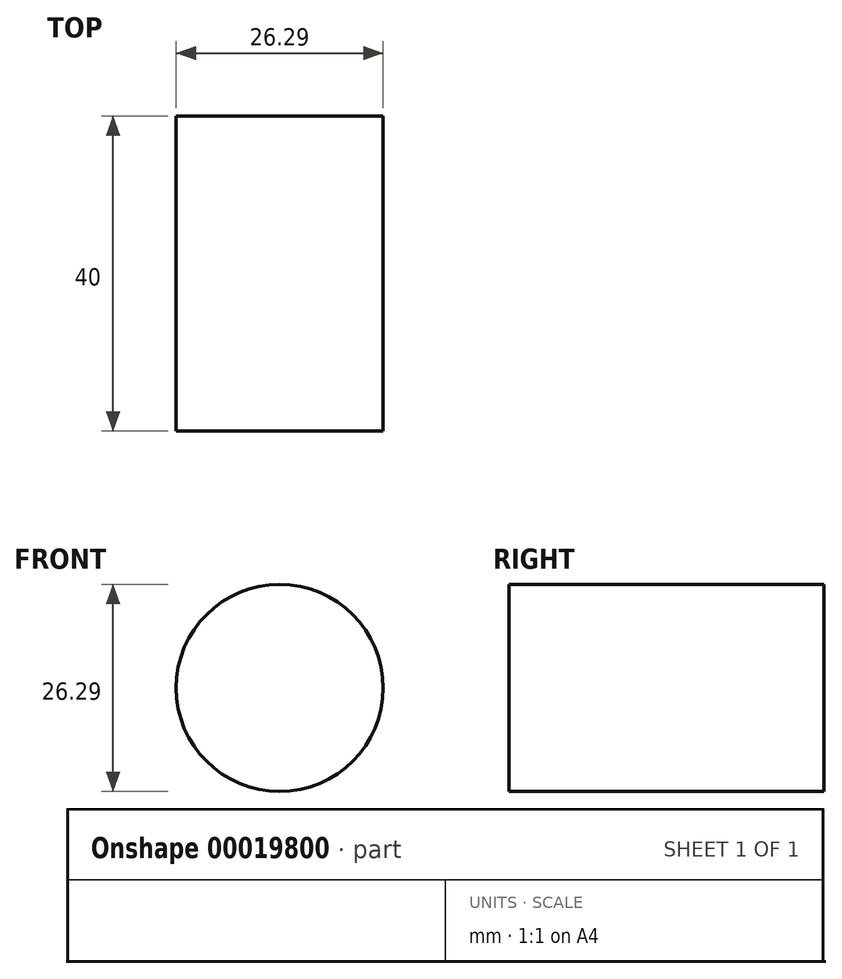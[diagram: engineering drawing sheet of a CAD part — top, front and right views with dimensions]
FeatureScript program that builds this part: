
annotation { "Feature Type Name" : "Feature", "Feature Type Description" : "" }
export const myFeature = defineFeature(function(context is Context, id is Id, definition is map)
    precondition{}
    {
        {
            var Q0;
            Q0=qCreatedBy(makeId("Front.planeOp"),FACE);
            var sketch = newSketch(context, id + "F0", { "sketchPlane" : qUnion([Q0])});
            skCircle(sketch, "E0", {"center": v(-22.02, 36.82) * mm, "radius": 13.15 * mm});
            skSolve(sketch);
        }
        {
            var Q0;
            Q0=makeQuery(id+"F0.imprint","IMPRINT",FACE,{"disambiguationData":[TD([[makeQuery(id+"F0.imprint","IMPRINT",EDGE,{"derivedFrom":sQuery(id+"F0.wireOp",EDGE,"E0")}),1.0]])]});
            extrude(context, id + "F1", {"entities" : qUnion([Q0]), "depth" : 40 * mm});
        }
    });
